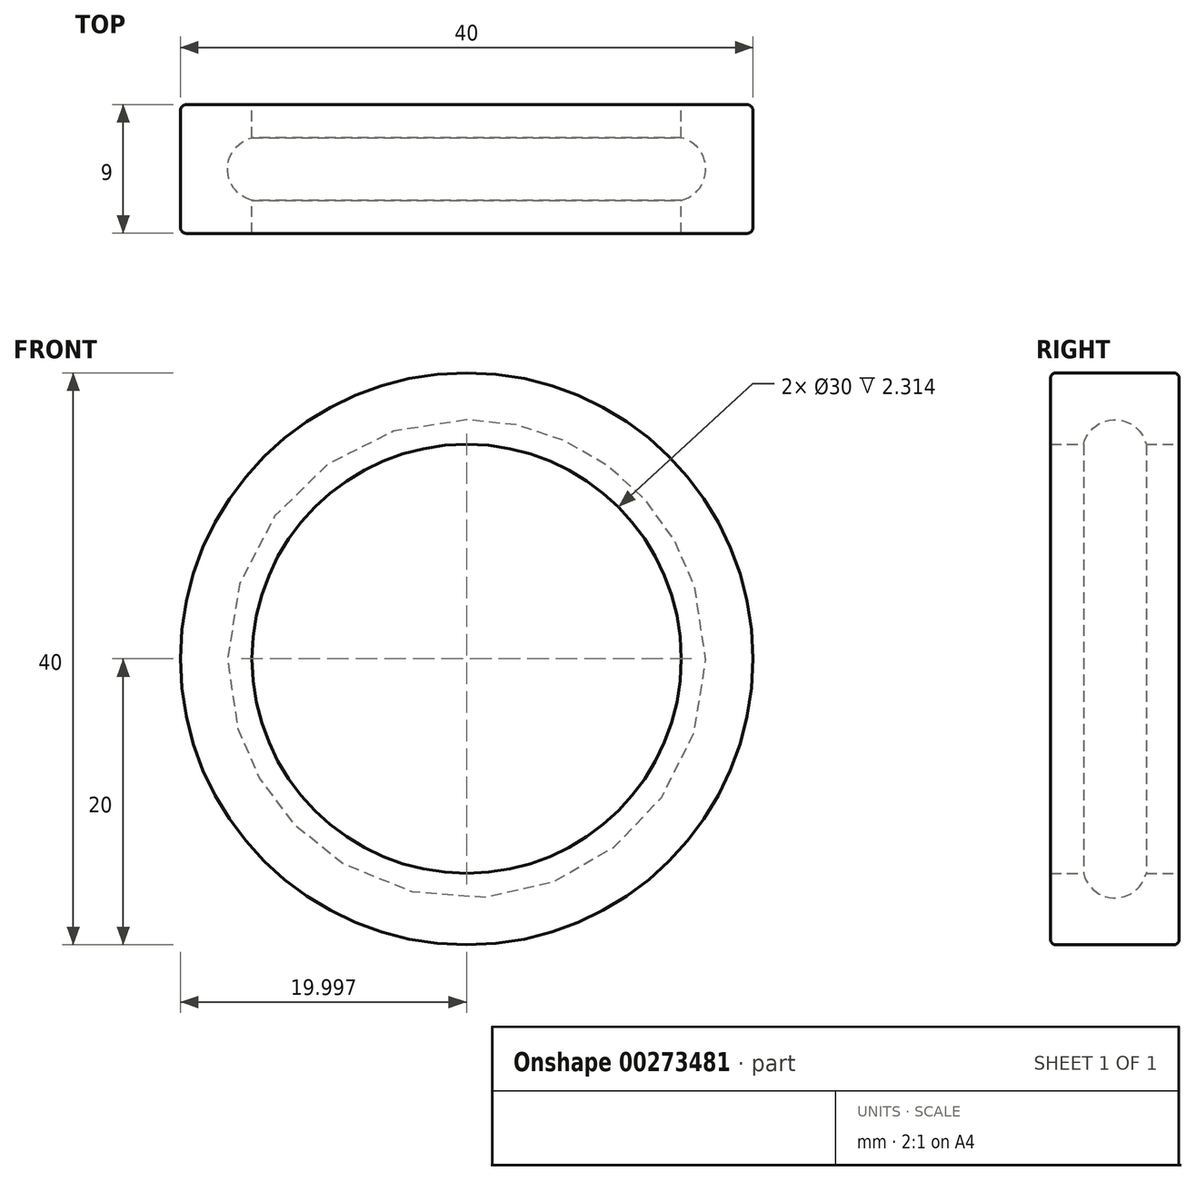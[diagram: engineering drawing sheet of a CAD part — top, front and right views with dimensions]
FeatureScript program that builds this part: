
annotation { "Feature Type Name" : "Feature", "Feature Type Description" : "" }
export const myFeature = defineFeature(function(context is Context, id is Id, definition is map)
    precondition{}
    {
        {
            var Q0;
            Q0=qCreatedBy(makeId("Top.planeOp"),FACE);
            var sketch = newSketch(context, id + "F0", { "sketchPlane" : qUnion([Q0])});
            skLineSegment(sketch, "E0", {"start": v(4.87, 9.93) * mm, "end": v(9.37, 9.93) * mm});
            skLineSegment(sketch, "E1", {"start": v(9.37, 9.93) * mm, "end": v(9.87, 9.93) * mm});
            skLineSegment(sketch, "E2", {"start": v(9.87, 9.93) * mm, "end": v(9.87, 12.24) * mm});
            skLineSegment(sketch, "E3", {"start": v(9.87, 18.93) * mm, "end": v(4.87, 18.93) * mm});
            skLineSegment(sketch, "E4", {"start": v(4.87, 18.93) * mm, "end": v(4.87, 9.93) * mm});
            skArc(sketch, "E5", {"start": v(9.87, 16.61) * mm, "mid": v(8.15, 14.43) * mm, "end": v(9.87, 12.24) * mm});
            skPoint(sketch, "E5.centerSnap0", {"position": v(9.87, 14.43) * mm});
            skLineSegment(sketch, "E6", {"start": v(24.87, 18.93) * mm, "end": v(24.87, 9.93) * mm});
            skLineSegment(sketch, "E7.trimOffspring", {"start": v(9.87, 16.61) * mm, "end": v(9.87, 18.93) * mm});
            skSolve(sketch);
        }
        {
            var Q0;
            Q0 = qSketchRegion(id + "F0", true);
            var Q1;
            Q1=sQuery(id+"F0.wireOp",EDGE,"E6");
            revolve(context, id + "F1", {"entities" : qUnion([Q0]), "axis" : qUnion([Q1]), "revolveType" : RevolveType.FULL});
        }
        {
            var Q0;
            Q0=makeQuery(id+"F1.opRevolve","SWEPT_EDGE",EDGE,{"disambiguationData":[OSD([sQuery(id+"F0.wireOp",EDGE,"E3"),sQuery(id+"F0.wireOp",EDGE,"E4")])]});
            var Q1;
            Q1=makeQuery(id+"F1.opRevolve","SWEPT_EDGE",EDGE,{"disambiguationData":[OSD([sQuery(id+"F0.wireOp",EDGE,"E0"),sQuery(id+"F0.wireOp",EDGE,"E4")])]});
            fillet(context, id + "F2", {"entities" : qUnion([Q0, Q1]), "radius" : 0.4 * mm, "tangentPropagation" : true, "allowEdgeOverflow" : false});
        }
    });
